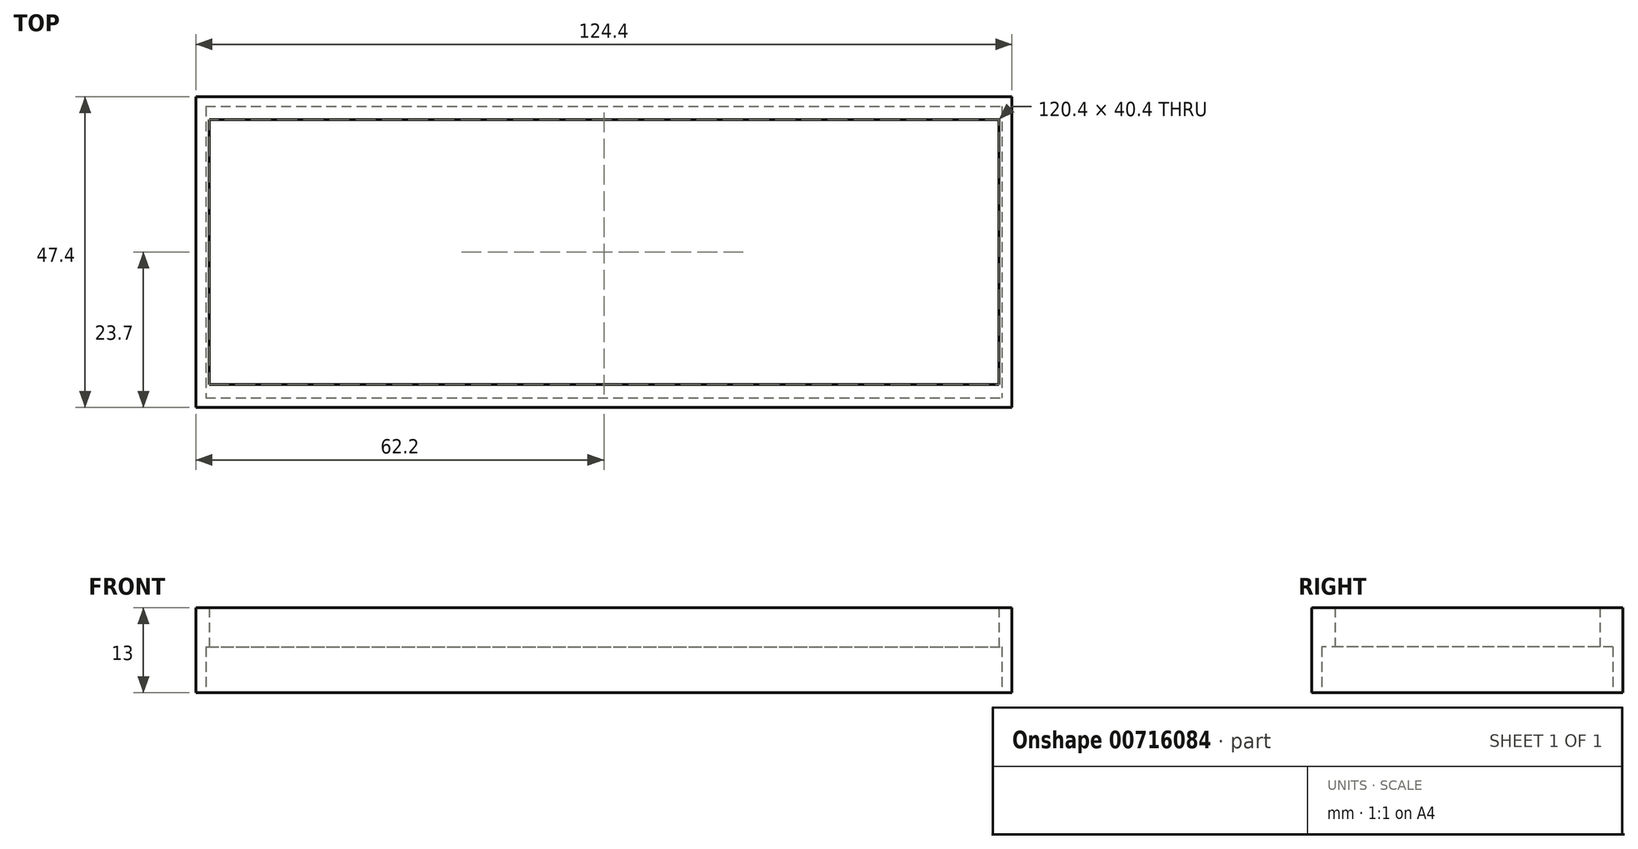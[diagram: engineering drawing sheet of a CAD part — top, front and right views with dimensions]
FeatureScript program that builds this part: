
annotation { "Feature Type Name" : "Feature", "Feature Type Description" : "" }
export const myFeature = defineFeature(function(context is Context, id is Id, definition is map)
    precondition{}
    {
        {
            var Q0;
            Q0=qCreatedBy(makeId("Top.planeOp"),FACE);
            var sketch = newSketch(context, id + "F0", { "sketchPlane" : qUnion([Q0])});
            skLineSegment(sketch, "E0.bottom", {"start": v(-60.7, 22.2) * mm, "end": v(60.7, 22.2) * mm});
            skLineSegment(sketch, "E0.top", {"start": v(-60.7, -22.2) * mm, "end": v(60.7, -22.2) * mm});
            skLineSegment(sketch, "E0.left", {"start": v(-60.7, 22.2) * mm, "end": v(-60.7, -22.2) * mm});
            skLineSegment(sketch, "E0.right", {"start": v(60.7, 22.2) * mm, "end": v(60.7, -22.2) * mm});
            skPoint(sketch, "E0.middle", {"position": v(0, 0) * mm});
            skLineSegment(sketch, "E1.bottom", {"start": v(-62.2, 23.7) * mm, "end": v(62.2, 23.7) * mm});
            skLineSegment(sketch, "E1.top", {"start": v(-62.2, -23.7) * mm, "end": v(62.2, -23.7) * mm});
            skLineSegment(sketch, "E1.left", {"start": v(-62.2, 23.7) * mm, "end": v(-62.2, -23.7) * mm});
            skLineSegment(sketch, "E1.right", {"start": v(62.2, 23.7) * mm, "end": v(62.2, -23.7) * mm});
            skSolve(sketch);
        }
        {
            var Q0;
            Q0=makeQuery(id+"F0.imprint","IMPRINT",FACE,{"disambiguationData":[TD([[makeQuery(id+"F0.imprint","IMPRINT",EDGE,{"derivedFrom":sQuery(id+"F0.wireOp",EDGE,"E0.bottom")}),1.0]])]});
            extrude(context, id + "F1", {"entities" : qUnion([Q0]), "depth" : 7 * mm, "offsetDistance" : 25 * mm});
        }
        {
            var Q0;
            Q0=makeQuery(id+"F1.opExtrude","CAP_FACE",FACE,{"disambiguationData":[OSD([sQuery(id+"F0.wireOp",EDGE,"E0.bottom"),sQuery(id+"F0.wireOp",EDGE,"E0.top"),sQuery(id+"F0.wireOp",EDGE,"E0.left"),sQuery(id+"F0.wireOp",EDGE,"E0.right"),sQuery(id+"F0.wireOp",EDGE,"E1.bottom"),sQuery(id+"F0.wireOp",EDGE,"E1.top"),sQuery(id+"F0.wireOp",EDGE,"E1.left"),sQuery(id+"F0.wireOp",EDGE,"E1.right")])],"isStart":false});
            var sketch = newSketch(context, id + "F2", { "sketchPlane" : qUnion([Q0])});
            skLineSegment(sketch, "E2.bottom", {"start": v(-60.2, 20.2) * mm, "end": v(60.2, 20.2) * mm});
            skLineSegment(sketch, "E2.top", {"start": v(-60.2, -20.2) * mm, "end": v(60.2, -20.2) * mm});
            skLineSegment(sketch, "E2.left", {"start": v(-60.2, 20.2) * mm, "end": v(-60.2, -20.2) * mm});
            skLineSegment(sketch, "E2.right", {"start": v(60.2, 20.2) * mm, "end": v(60.2, -20.2) * mm});
            skPoint(sketch, "E2.middle", {"position": v(0, 0) * mm});
            skLineSegment(sketch, "E3.bottom", {"start": v(-269.28, 120.7) * mm, "end": v(269.28, 120.7) * mm});
            skLineSegment(sketch, "E3.top", {"start": v(-269.28, -120.7) * mm, "end": v(269.28, -120.7) * mm});
            skLineSegment(sketch, "E3.left", {"start": v(-269.28, 120.7) * mm, "end": v(-269.28, -120.7) * mm});
            skLineSegment(sketch, "E3.right", {"start": v(269.28, 120.7) * mm, "end": v(269.28, -120.7) * mm});
            skLineSegment(sketch, "E4.bottom", {"start": v(-62.2, 23.7) * mm, "end": v(62.2, 23.7) * mm});
            skLineSegment(sketch, "E4.top", {"start": v(-62.2, -23.7) * mm, "end": v(62.2, -23.7) * mm});
            skLineSegment(sketch, "E4.left", {"start": v(-62.2, 23.7) * mm, "end": v(-62.2, -23.7) * mm});
            skLineSegment(sketch, "E4.right", {"start": v(62.2, 23.7) * mm, "end": v(62.2, -23.7) * mm});
            skSolve(sketch);
        }
        {
            var Q0;
            Q0=makeQuery(id+"F2.imprint","IMPRINT",FACE,{"disambiguationData":[TD([[makeQuery(id+"F2.imprint","IMPRINT",EDGE,{"derivedFrom":sQuery(id+"F2.wireOp",EDGE,"E2.bottom")}),1.0]])]});
            var Q1;
            Q1=makeQuery(id+"F2.imprint","IMPRINT",FACE,{"disambiguationData":[TD([[makeQuery(id+"F2.imprint","IMPRINT",EDGE,{"derivedFrom":sQuery(id+"F2.wireOp",EDGE,"E4.bottom")}),-1.0]])]});
            extrude(context, id + "F3", {"entities" : qUnion([Q0, Q1]), "operationType" : NewBodyOperationType.ADD, "depth" : 6 * mm, "offsetDistance" : 25 * mm});
        }
    });
